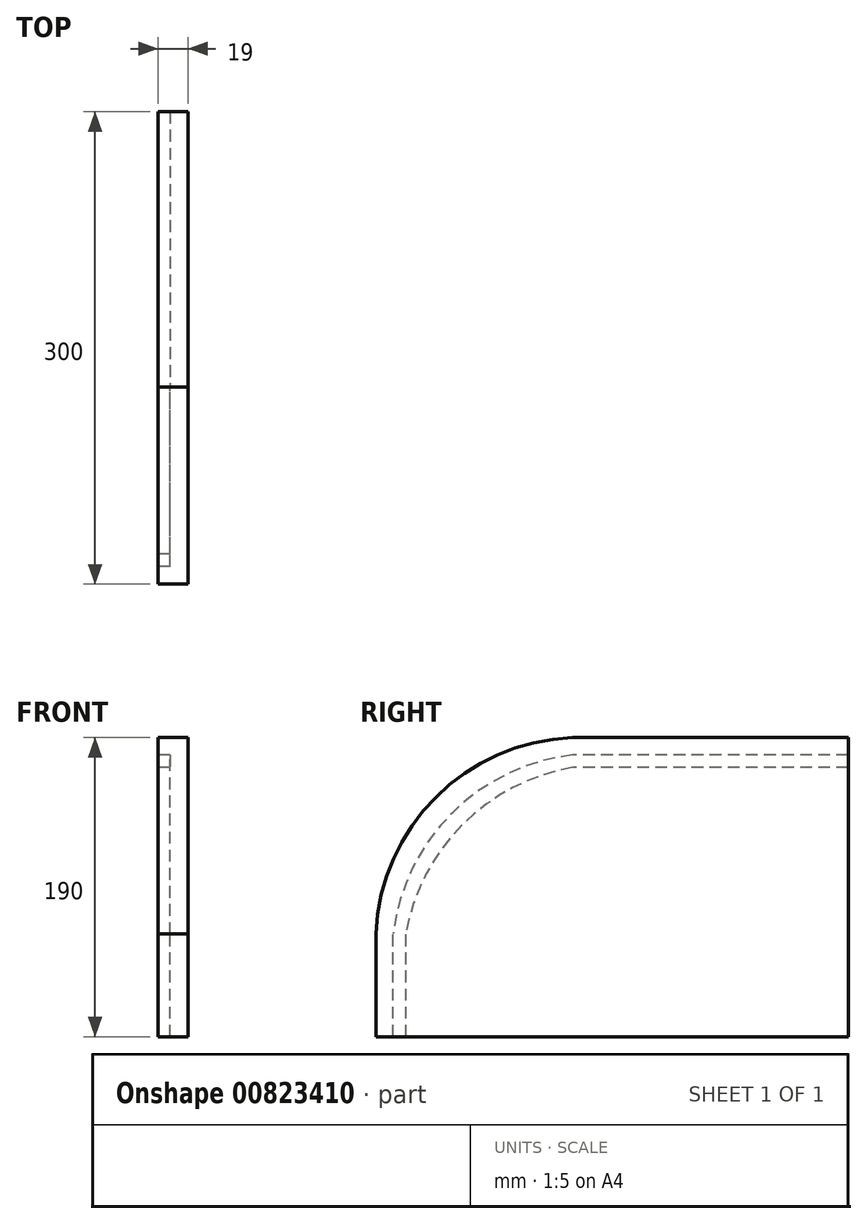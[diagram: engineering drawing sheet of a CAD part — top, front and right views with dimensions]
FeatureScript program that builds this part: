
annotation { "Feature Type Name" : "Feature", "Feature Type Description" : "" }
export const myFeature = defineFeature(function(context is Context, id is Id, definition is map)
    precondition{}
    {
        {
            var Q0;
            Q0=qCreatedBy(makeId("Right.planeOp"),FACE);
            var sketch = newSketch(context, id + "F0", { "sketchPlane" : qUnion([Q0])});
            skLineSegment(sketch, "E0.bottom", {"start": v(-25, 95) * mm, "end": v(150, 95) * mm});
            skLineSegment(sketch, "E0.top", {"start": v(-150, -95) * mm, "end": v(150, -95) * mm});
            skLineSegment(sketch, "E0.left", {"start": v(-150, -29.82) * mm, "end": v(-150, -95) * mm});
            skLineSegment(sketch, "E0.right", {"start": v(150, 95) * mm, "end": v(150, -95) * mm});
            skPoint(sketch, "E0.middle", {"position": v(0, 0) * mm});
            skPoint(sketch, "E1", {"position": v(-150, -40) * mm});
            skPoint(sketch, "E2", {"position": v(-25, 95) * mm});
            skArc(sketch, "E3", {"start": v(-25, 95) * mm, "mid": v(-115.49, 53.42) * mm, "end": v(-150, -40) * mm});
            skPoint(sketch, "E4.orphan", {"position": v(-150, 95) * mm});
            skSolve(sketch);
        }
        {
            var Q0;
            {var subQ5=sQuery(id+"F0.wireOp",EDGE,"E0.bottom");Q0=makeQuery(id+"F0.imprint","IMPRINT",FACE,{"disambiguationData":[TD([[makeQuery(id+"F0.imprint","IMPRINT",EDGE,{"derivedFrom":subQ5}),-1.0]])]});}
            extrude(context, id + "F1", {"entities" : qUnion([Q0]), "flatOperationType" : FlatOperationType.REMOVE, "depth" : 19 * mm, "offsetDistance" : 25 * mm, "domain" : OperationDomain.MODEL});
        }
        {
            var Q0;
            Q0=makeQuery(id+"F1.opExtrude","CAP_FACE",FACE,{"disambiguationData":[OSD([sQuery(id+"F0.wireOp",EDGE,"E0.bottom"),sQuery(id+"F0.wireOp",EDGE,"E0.top"),sQuery(id+"F0.wireOp",EDGE,"E0.left"),sQuery(id+"F0.wireOp",EDGE,"E0.right"),sQuery(id+"F0.wireOp",EDGE,"E3")])],"isStart":true});
            var sketch = newSketch(context, id + "F2", { "sketchPlane" : qUnion([Q0])});
            skPoint(sketch, "E5", {"position": v(-150, 84) * mm});
            skLineSegment(sketch, "E6", {"start": v(-150, 84) * mm, "end": v(25, 84) * mm});
            skPoint(sketch, "E7", {"position": v(-150, 76) * mm});
            skLineSegment(sketch, "E8", {"start": v(-150, 76) * mm, "end": v(25, 76) * mm});
            skPoint(sketch, "E9", {"position": v(139, -95) * mm});
            skPoint(sketch, "E10", {"position": v(131, -95) * mm});
            skLineSegment(sketch, "E11", {"start": v(139, -95) * mm, "end": v(139, -29.82) * mm});
            skLineSegment(sketch, "E12", {"start": v(131, -95) * mm, "end": v(131, -29.82) * mm});
            skArc(sketch, "E13", {"start": v(139, -29.82) * mm, "mid": v(101.75, 46.88) * mm, "end": v(25, 84) * mm});
            skArc(sketch, "E14", {"start": v(131, -29.82) * mm, "mid": v(94.77, 39.9) * mm, "end": v(25, 76) * mm});
            skSolve(sketch);
        }
        {
            var Q0;
            {var subQ1=sQuery(id+"F2.wireOp",EDGE,"E6");Q0=makeQuery(id+"F2.imprint","IMPRINT",FACE,{"disambiguationData":[TD([[makeQuery(id+"F2.imprint","IMPRINT",EDGE,{"derivedFrom":subQ1}),-1.0]])]});}
            extrude(context, id + "F3", {"entities" : qUnion([Q0]), "operationType" : NewBodyOperationType.REMOVE, "oppositeDirection" : true, "depth" : 7.5 * mm, "offsetDistance" : 25 * mm});
        }
    });
